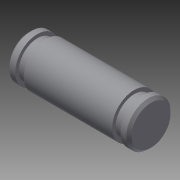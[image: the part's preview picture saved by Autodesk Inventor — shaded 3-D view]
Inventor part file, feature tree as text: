
AUTODESK INVENTOR PART (.ipt)
format: ipt  version: 2014 SP2 (Build 180246200, 246)  size: 124,928 bytes
history: native  units: in
note: dims shown in document units (in); Inventor stores cm internally (conversion verified against a paired STEP export)
features: other x49, revolve x1, sketch x1
ambient origin geometry x8: Origin, YZ Plane, XZ Plane, XY Plane, X Axis, Y Axis, Z Axis, Center Point
bodies: Solid1 (feature_tree)
feature tree (51):
  revolve  "Revolution1"  [1 undecoded]
  other  "p1_XY"
  other  "p1_YZ"
  other  "p1_ZX"
  other  "p1_X"
  other  "p1_Y"
  other  "p1_Z"
  other  "p1_Center"
  other  "p2_XY"
  other  "p2_YZ"
  other  "p2_ZX"
  other  "p2_X"
  other  "p2_Y"
  other  "p2_Z"
  other  "p2_Center"
  other  "pin_XY"
  other  "pin_YZ"
  other  "pin_ZX"
  other  "pin_X"
  other  "pin_Y"
  other  "pin_Z"
  other  "pin_Center"
  other  "rr1_XY"
  other  "rr1_YZ"
  other  "rr1_ZX"
  other  "rr1_X"
  other  "rr1_Y"
  other  "rr1_Z"
  other  "rr1_Center"
  other  "rr2_XY"
  other  "rr2_YZ"
  other  "rr2_ZX"
  other  "rr2_X"
  other  "rr2_Y"
  other  "rr2_Z"
  other  "rr2_Center"
  other  "w21_XY"
  other  "w21_YZ"
  other  "w21_ZX"
  other  "w21_X"
  other  "w21_Y"
  other  "w21_Z"
  other  "w21_Center"
  other  "w22_XY"
  other  "w22_YZ"
  other  "w22_ZX"
  other  "w22_X"
  other  "w22_Y"
  other  "w22_Z"
  other  "w22_Center"
  sketch  "Sketch_1"  dims[d0=360.0deg]
note: 1 required parameter value undecoded (feature->parameter linkage not recoverable at this tier; creation-order binding heuristic only, values carry confidence <= 0.55)
